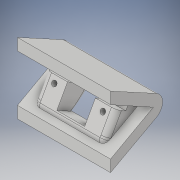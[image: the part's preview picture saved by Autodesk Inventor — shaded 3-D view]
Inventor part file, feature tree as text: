
AUTODESK INVENTOR PART (.ipt)
format: ipt  version: 2018 (Build 220112000, 112)  size: 498,176 bytes
history: native  units: in
note: dims shown in document units (in); Inventor stores cm internally (conversion verified against a paired STEP export)
features: extrude x18, sketch x16, fillet x12, plane x8, split x4, shell x1, chamfer x1
ambient origin geometry x8: Origin, YZ Plane, XZ Plane, XY Plane, X Axis, Y Axis, Z Axis, Center Point
bodies: Solid1 (feature_tree)
feature tree (60):
  extrude  "Extrusion1"  Depth=4.4094in
  shell  "Shell1"  Thickness=7.6772in
  extrude  "Extrusion8"  Depth=0.25in
  fillet  "Fillet3"  Radius=0.25in
  sketch  "Sketch10"  dims[d54=0.25in d55=0.25in]
  extrude  "Extrusion10"  Depth=0.25in
  extrude  "Extrusion11"  Depth=0.25in
  fillet  "Fillet14"  Radius=1.0in
  extrude  "Extrusion12"  Depth=0.125in
  plane  "Work Plane2"
  extrude  "Extrusion13"  Depth=0.125in
  plane  "Work Plane4"
  extrude  "Extrusion26"  Depth=0.125in
  extrude  "Extrusion27"  TaperAngle=0.0deg  [1 undecoded]
  fillet  "Fillet15"  [1 undecoded]
  plane  "Work Plane6"
  extrude  "Extrusion28"  Depth=0.1181in
  plane  "Work Plane7"
  extrude  "Extrusion29"  Depth=0.1181in
  extrude  "Extrusion30"  Depth=10.0in TaperAngle=0.0deg
  extrude  "Extrusion31"  Depth=10.0in TaperAngle=0.0deg
  extrude  "Extrusion32"  [1 undecoded]
  fillet  "Fillet16"  Radius=0.2756in
  fillet  "Fillet18"  Radius=0.2756in
  fillet  "Fillet19"  Radius=0.2756in
  extrude  "Extrusion33"  Depth=0.45in TaperAngle=0.0deg
  plane  "Work Plane8"
  split  "Split1"
  plane  "Work Plane9"
  split  "Split2"
  plane  "Work Plane10"
  plane  "Work Plane11"
  split  "Split3"
  split  "Split4"
  extrude  "Extrusion34"  Depth=0.1969in
  extrude  "Extrusion35"  Depth=0.1575in
  fillet  "Fillet21"  Radius=5.0in
  extrude  "Extrusion36"  Depth=0.1575in
  chamfer  "Chamfer2"  Distance=0.5in
  extrude  "Extrusion37"  Depth=0.125in
  fillet  "Fillet22"  Radius=0.125in
  fillet  "Fillet23"  Radius=0.125in
  fillet  "Fillet24"  Radius=0.125in
  fillet  "Fillet25"  Radius=0.125in
  fillet  "Fillet26"  Radius=0.125in
  sketch  "Sketch1"  dims[d0=4.0in d1=4.4094in d2=7.6772in d3=0.0in]
  sketch  "Sketch9"  dims[d4=0.25in d52=0.25in d53=0.25in]
  sketch  "Sketch11"  dims[d56=0.25in d57=0.25in d58=1.0in d59=0.0in]
  sketch  "Sketch12"  dims[d60=0.125in d61=0.125in]
  sketch  "Sketch13"  dims[d62=0.125in d63=0.125in]
  sketch  "Sketch26"  dims[d64=0.125in d65=1.2894in]
  sketch  "Sketch27"  dims[d66=5.0in d67=0.0in d68=0.0in]
  sketch  "Sketch31"  dims[d69=0.1181in d71=0.1181in]
  sketch  "Sketch32"  dims[d72=0.1181in d76=0.1181in]
  sketch  "Sketch33"  dims[d81=1.0in d82=0.0in d85=10.0in d86=0.0in]
  sketch  "Sketch35"  dims[d88=0.315in d89=10.0in d90=0.0in]
  sketch  "Sketch36"  dims[d99=0.2756in d100=-0.5in d101=0.2756in d102=0.2756in d103=0.2756in]
  sketch  "Sketch37"  dims[d104=0.2756in d105=0.45in d106=0.0in]
  sketch  "Sketch39"  dims[d154=90.0deg d155=0.1969in]
  sketch  "Sketch40"  dims[d156=0.5157in d157=0.6496in d158=5.0in d159=0.0in d160=1.0in d161=0.5in d162=0.125in d163=0.125in d164=0.125in d165=0.125in d166=0.125in d167=0.125in d168=0.25in d169=0.25in d170=0.5in d171=0.5in d172=0.5in d173=0.5in d174=0.5in d175=0.0in d176=0.0625in d181=90.0deg d182=0.125in d183=0.5in d184=0.5in d185=4.7in d186=0.0in d187=90.0deg d188=4.7in d189=0.0in d190=4.0in d191=0.0in d192=0.242in d193=0.0in d196=0.1181in d197=0.1181in d198=0.1575in d199=0.0in d200=0.0625in d203=0.0394in d204=0.0394in d206=0.6in d207=0.0in d208=-0.4in d209=-3.0in d210=1.136in d211=0.2568in d212=0.2568in d213=0.256in d214=0.2579in d215=-3.0in d216=-3.0in d217=0.1969in d218=2.3622in d219=1.5748in d220=0.0in d221=0.1181in d222=0.0in d223=0.2657in d224=0.6102in d229=0.0787in d230=0.0787in d231=0.0787in d232=0.0787in d233=0.0787in d234=0.0in d236=0.125in d237=0.0394in d238=0.0394in d239=0.0394in d240=0.1181in d241=0.0in d242=0.1181in d243=0.125in d244=45.0deg d245=0.9646in d246=1.3583in d247=0.1969in d248=0.1969in d249=0.1969in d250=0.1969in d251=0.0394in d252=0.0in d253=0.0394in d254=0.3937in d255=0.125in d256=0.125in d257=0.1575in d258=0.1575in d259=0.1575in]
note: 3 required parameter values undecoded (feature->parameter linkage not recoverable at this tier; creation-order binding heuristic only, values carry confidence <= 0.55)
